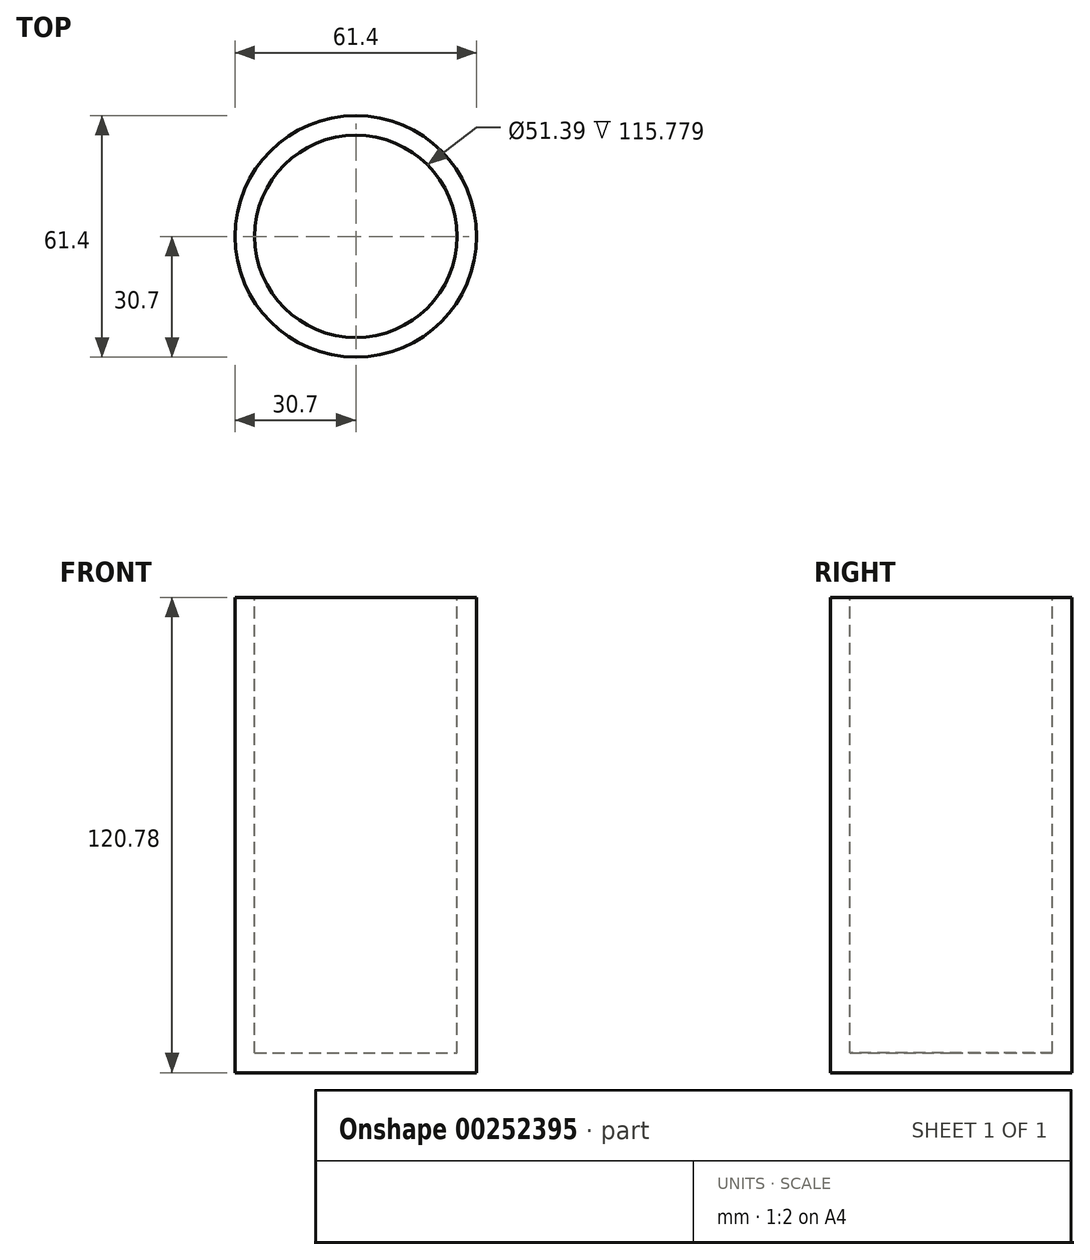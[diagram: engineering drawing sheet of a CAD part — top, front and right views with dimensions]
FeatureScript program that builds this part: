
annotation { "Feature Type Name" : "Feature", "Feature Type Description" : "" }
export const myFeature = defineFeature(function(context is Context, id is Id, definition is map)
    precondition{}
    {
        {
            var Q0;
            Q0=qCreatedBy(makeId("Front.planeOp"),FACE);
            var sketch = newSketch(context, id + "F0", { "sketchPlane" : qUnion([Q0])});
            skLineSegment(sketch, "E0.bottom", {"start": v(-30.7, -60.39) * mm, "end": v(30.7, -60.39) * mm});
            skLineSegment(sketch, "E0.top", {"start": v(-30.7, 60.39) * mm, "end": v(30.7, 60.39) * mm});
            skLineSegment(sketch, "E0.left", {"start": v(-30.7, -60.39) * mm, "end": v(-30.7, 60.39) * mm});
            skLineSegment(sketch, "E0.right", {"start": v(30.7, -60.39) * mm, "end": v(30.7, 60.39) * mm});
            skPoint(sketch, "E0.middle", {"position": v(0, 0) * mm});
            skLineSegment(sketch, "E1", {"start": v(0, 60.39) * mm, "end": v(0, -60.39) * mm});
            skSolve(sketch);
        }
        {
            var Q0;
            {var subQ0=sQuery(id+"F0.wireOp",EDGE,"E0.left");Q0=makeQuery(id+"F0.imprint","IMPRINT",FACE,{"disambiguationData":[TD([[makeQuery(id+"F0.imprint","IMPRINT",EDGE,{"derivedFrom":subQ0}),-1.0]])]});}
            var Q1;
            Q1=sQuery(id+"F0.wireOp",EDGE,"E1");
            revolve(context, id + "F1", {"entities" : qUnion([Q0]), "axis" : qUnion([Q1]), "revolveType" : RevolveType.FULL});
        }
        {
            var Q0;
            Q0=makeQuery(id+"F1.opRevolve","SWEPT_FACE",FACE,{"disambiguationData":[OSD([sQuery(id+"F0.wireOp",EDGE,"E0.top")])]});
            shell(context, id + "F2", {"entities" : qUnion([Q0]), "thickness" : 5 * mm});
        }
    });
